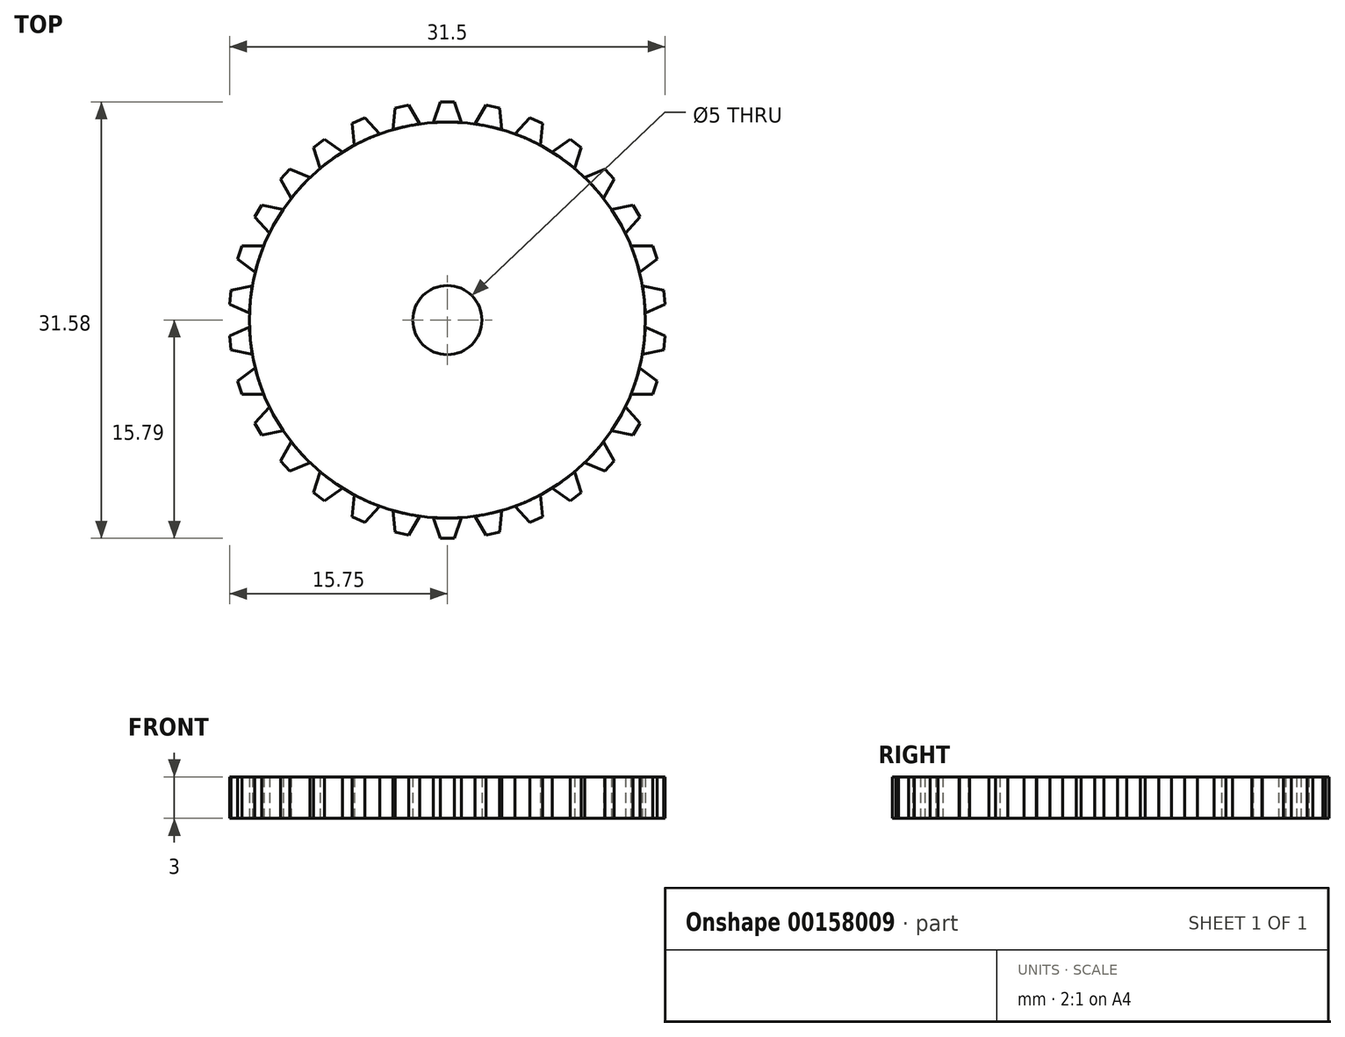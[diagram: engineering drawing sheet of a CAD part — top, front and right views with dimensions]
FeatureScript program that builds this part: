
annotation { "Feature Type Name" : "Feature", "Feature Type Description" : "" }
export const myFeature = defineFeature(function(context is Context, id is Id, definition is map)
    precondition{}
    {
        {
            var Q0;
            Q0=qCreatedBy(makeId("Top.planeOp"),FACE);
            var sketch = newSketch(context, id + "F0", { "sketchPlane" : qUnion([Q0])});
            skCircle(sketch, "E0", {"center": v(0, 0) * mm, "radius": 14.32 * mm});
            skCircle(sketch, "E1", {"center": v(0, 0) * mm, "radius": 2.5 * mm});
            skSolve(sketch);
        }
        {
            var Q0;
            Q0=makeQuery(id+"F0.imprint","IMPRINT",FACE,{"disambiguationData":[TD([[makeQuery(id+"F0.imprint","IMPRINT",EDGE,{"derivedFrom":sQuery(id+"F0.wireOp",EDGE,"E0")}),1.0]])]});
            var sketch = newSketch(context, id + "F1", { "sketchPlane" : qUnion([Q0])});
            skCircle(sketch, "E2.0", {"center": v(0, 0) * mm, "radius": 14.32 * mm});
            skLineSegment(sketch, "E3", {"start": v(-1, 14.29) * mm, "end": v(-0.5, 15.79) * mm});
            skLineSegment(sketch, "E4", {"start": v(-0.5, 15.79) * mm, "end": v(0.5, 15.79) * mm});
            skLineSegment(sketch, "E5", {"start": v(0.5, 15.79) * mm, "end": v(1, 14.29) * mm});
            skSolve(sketch);
        }
        {
            var Q0;
            Q0=makeQuery(id+"F0.imprint","IMPRINT",FACE,{"disambiguationData":[TD([[makeQuery(id+"F0.imprint","IMPRINT",EDGE,{"derivedFrom":sQuery(id+"F0.wireOp",EDGE,"E0")}),1.0]])]});
            extrude(context, id + "F2", {"entities" : qUnion([Q0]), "depth" : 3 * mm});
        }
        {
            var Q0;
            {var subQ0=sQuery(id+"F1.wireOp",EDGE,"E3");Q0=makeQuery(id+"F1.imprint","IMPRINT",FACE,{"disambiguationData":[TD([[makeQuery(id+"F1.imprint","IMPRINT",EDGE,{"derivedFrom":subQ0}),-1.0]])]});}
            extrude(context, id + "F3", {"entities" : qUnion([Q0]), "depth" : 3 * mm});
        }
        {
            var Q0;
            Q0=makeQuery(id+"F3.opExtrude","SWEPT_BODY",BODY,{"disambiguationData":[OSD([sQuery(id+"F1.wireOp",EDGE,"E2.0"),sQuery(id+"F1.wireOp",EDGE,"E3"),sQuery(id+"F1.wireOp",EDGE,"E4"),sQuery(id+"F1.wireOp",EDGE,"E5")])]});
            var Q1;
            Q1=makeQuery(id+"F2.opExtrude","SWEPT_FACE",FACE,{"disambiguationData":[OSD([sQuery(id+"F0.wireOp",EDGE,"E0")])]});
            circularPattern(context, id + "F4", {"entities" : qUnion([Q0]), "axis" : qUnion([Q1]), "angle" : 12 * degree, "instanceCount" : 30});
        }
    });
